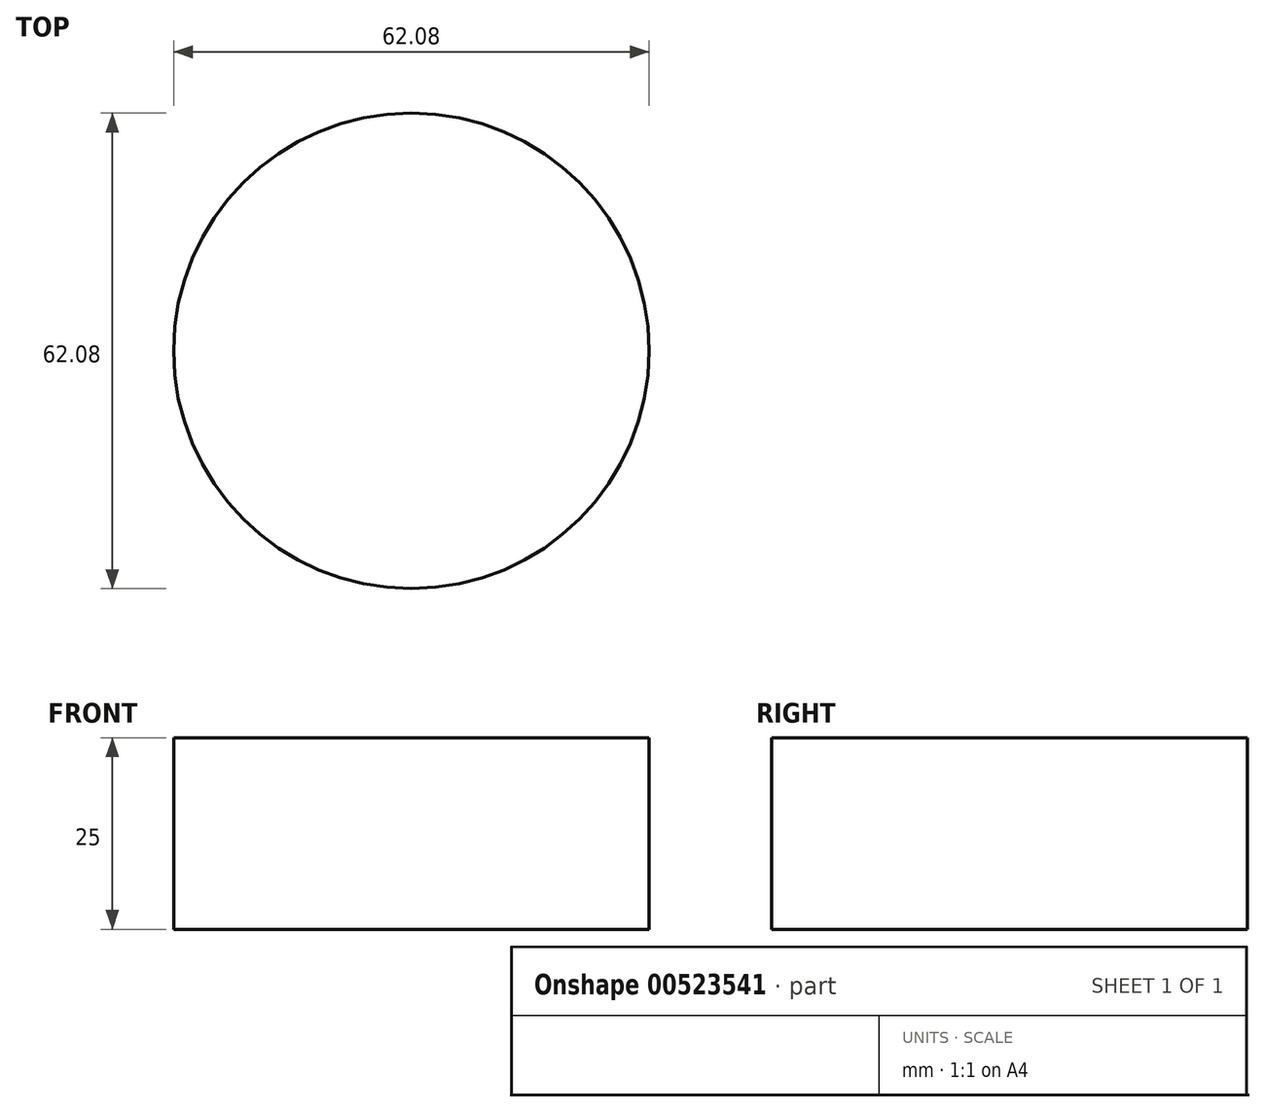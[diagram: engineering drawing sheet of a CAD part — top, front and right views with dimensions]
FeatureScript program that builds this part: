
annotation { "Feature Type Name" : "Feature", "Feature Type Description" : "" }
export const myFeature = defineFeature(function(context is Context, id is Id, definition is map)
    precondition{}
    {
        {
            var Q0;
            Q0=qCreatedBy(makeId("Top.planeOp"),FACE);
            var sketch = newSketch(context, id + "F0", { "sketchPlane" : qUnion([Q0])});
            skCircle(sketch, "E0", {"center": v(0, 0) * mm, "radius": 31.04 * mm});
            skSolve(sketch);
        }
        {
            var Q0;
            Q0 = qSketchRegion(id + "F0", true);
            extrude(context, id + "F1", {"entities" : qUnion([Q0]), "depth" : 25 * mm, "offsetDistance" : 25 * mm});
        }
    });
